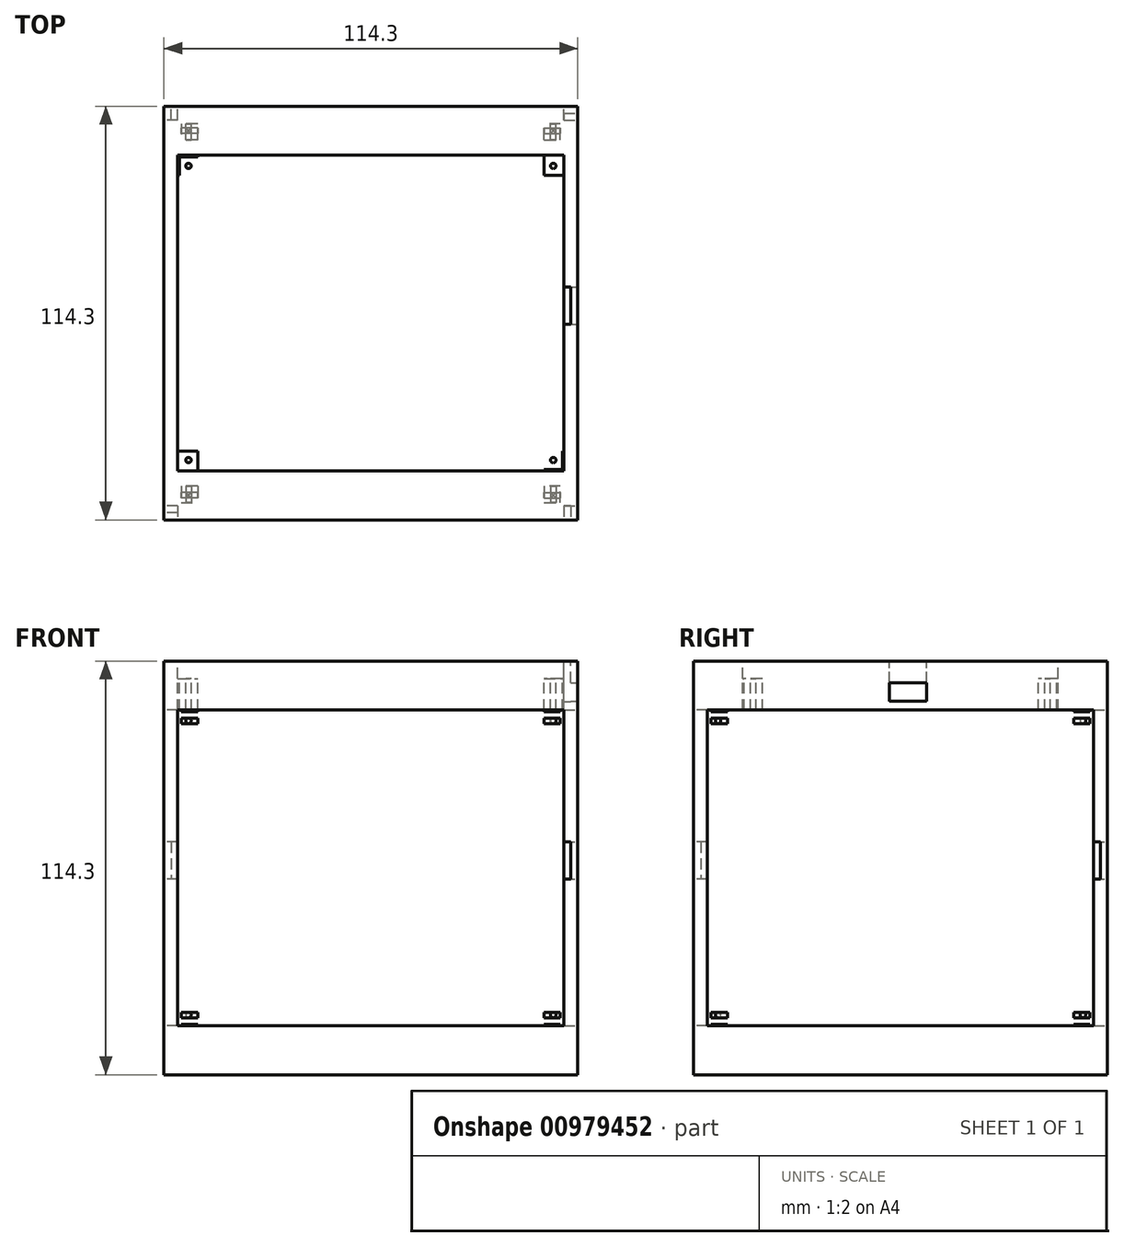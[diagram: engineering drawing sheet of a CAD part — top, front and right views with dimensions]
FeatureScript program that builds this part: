
annotation { "Feature Type Name" : "Feature", "Feature Type Description" : "" }
export const myFeature = defineFeature(function(context is Context, id is Id, definition is map)
    precondition{}
    {
        {
            var Q0;
            Q0=qCreatedBy(makeId("Top.planeOp"),FACE);
            var sketch = newSketch(context, id + "F0", { "sketchPlane" : qUnion([Q0])});
            skLineSegment(sketch, "E0.bottom", {"start": v(57.15, -57.15) * mm, "end": v(-57.15, -57.15) * mm});
            skLineSegment(sketch, "E0.top", {"start": v(57.15, 57.15) * mm, "end": v(-57.15, 57.15) * mm});
            skLineSegment(sketch, "E0.left", {"start": v(57.15, -57.15) * mm, "end": v(57.15, 57.15) * mm});
            skLineSegment(sketch, "E0.right", {"start": v(-57.15, -57.15) * mm, "end": v(-57.15, 57.15) * mm});
            skSolve(sketch);
        }
        {
            var Q0;
            Q0=makeQuery(id+"F0.imprint","IMPRINT",FACE,{"disambiguationData":[TD([[makeQuery(id+"F0.imprint","IMPRINT",EDGE,{"derivedFrom":sQuery(id+"F0.wireOp",EDGE,"E0.bottom")}),-1.0]])]});
            extrude(context, id + "F1", {"entities" : qUnion([Q0]), "depth" : 114.3 * mm, "offsetDistance" : 25.4 * mm});
        }
        {
            var Q0;
            Q0=makeQuery(id+"F1.opExtrude","CAP_FACE",FACE,{"disambiguationData":[OSD([sQuery(id+"F0.wireOp",EDGE,"E0.bottom"),sQuery(id+"F0.wireOp",EDGE,"E0.top"),sQuery(id+"F0.wireOp",EDGE,"E0.left"),sQuery(id+"F0.wireOp",EDGE,"E0.right")])],"isStart":false});
            var sketch = newSketch(context, id + "F2", { "sketchPlane" : qUnion([Q0])});
            skLineSegment(sketch, "E1.bottom", {"start": v(-52.92, 43.18) * mm, "end": v(52.92, 43.18) * mm});
            skLineSegment(sketch, "E1.top", {"start": v(-52.92, -43.18) * mm, "end": v(52.92, -43.18) * mm});
            skLineSegment(sketch, "E1.left", {"start": v(-52.92, 43.18) * mm, "end": v(-52.92, -43.18) * mm});
            skLineSegment(sketch, "E1.right", {"start": v(52.92, 43.18) * mm, "end": v(52.92, -43.18) * mm});
            skPoint(sketch, "E1.middle", {"position": v(0, 0) * mm});
            skCircle(sketch, "E2", {"center": v(-50.38, -40.64) * mm, "radius": 0.76 * mm});
            skCircle(sketch, "E3.MirrorC", {"center": v(50.38, -40.64) * mm, "radius": 0.76 * mm});
            skCircle(sketch, "E4.MirrorC", {"center": v(-50.38, 40.64) * mm, "radius": 0.76 * mm});
            skCircle(sketch, "E5.MirrorC", {"center": v(50.38, 40.64) * mm, "radius": 0.76 * mm});
            skLineSegment(sketch, "E6.0", {"start": v(-53.32, 43.58) * mm, "end": v(-53.32, -43.58) * mm});
            skLineSegment(sketch, "E6.1", {"start": v(-53.32, 43.58) * mm, "end": v(53.32, 43.58) * mm});
            skLineSegment(sketch, "E6.2", {"start": v(53.32, 43.58) * mm, "end": v(53.32, -43.58) * mm});
            skLineSegment(sketch, "E6.3", {"start": v(-53.32, -43.58) * mm, "end": v(53.32, -43.58) * mm});
            skLineSegment(sketch, "E7.top", {"start": v(53.32, -38.1) * mm, "end": v(47.84, -38.1) * mm});
            skLineSegment(sketch, "E7.right", {"start": v(47.84, -43.58) * mm, "end": v(47.84, -38.1) * mm});
            skLineSegment(sketch, "E8.MirrorCS", {"start": v(47.84, 43.58) * mm, "end": v(47.84, 38.1) * mm});
            skLineSegment(sketch, "E9.MirrorCS", {"start": v(53.32, 38.1) * mm, "end": v(47.84, 38.1) * mm});
            skLineSegment(sketch, "E10.MirrorCS", {"start": v(-53.32, -38.1) * mm, "end": v(-47.84, -38.1) * mm});
            skLineSegment(sketch, "E11.MirrorCS", {"start": v(-47.84, -43.58) * mm, "end": v(-47.84, -38.1) * mm});
            skLineSegment(sketch, "E12.MirrorCS", {"start": v(-53.32, 38.1) * mm, "end": v(-47.84, 38.1) * mm});
            skLineSegment(sketch, "E13.MirrorCS", {"start": v(-47.84, 43.58) * mm, "end": v(-47.84, 38.1) * mm});
            skLineSegment(sketch, "E14.MirrorCS", {"start": v(51.04, 6.8) * mm, "end": v(54.8, 6.8) * mm});
            skLineSegment(sketch, "E15.MirrorCS", {"start": v(51.04, -3.13) * mm, "end": v(55.2, -3.13) * mm});
            skLineSegment(sketch, "E16.MirrorCS", {"start": v(51.04, -2.73) * mm, "end": v(54.8, -2.73) * mm});
            skLineSegment(sketch, "E17.MirrorCS", {"start": v(55.2, 7.2) * mm, "end": v(55.2, -3.13) * mm});
            skLineSegment(sketch, "E18.MirrorCS", {"start": v(51.04, 7.2) * mm, "end": v(55.2, 7.2) * mm});
            skLineSegment(sketch, "E19.MirrorCS", {"start": v(54.8, 6.8) * mm, "end": v(54.8, -2.73) * mm});
            skPoint(sketch, "E20.MirrorP", {"position": v(52.92, 2.03) * mm});
            skLineSegment(sketch, "E21.bottom", {"start": v(-57.15, -57.15) * mm, "end": v(57.15, -57.15) * mm});
            skLineSegment(sketch, "E21.top", {"start": v(-57.15, 57.15) * mm, "end": v(57.15, 57.15) * mm});
            skLineSegment(sketch, "E21.left", {"start": v(-57.15, -57.15) * mm, "end": v(-57.15, 57.15) * mm});
            skLineSegment(sketch, "E21.right", {"start": v(57.15, -57.15) * mm, "end": v(57.15, 57.15) * mm});
            skSolve(sketch);
        }
        {
            var Q0;
            Q0=makeQuery(id+"F2.imprint","IMPRINT",FACE,{"disambiguationData":[TD([[makeQuery(id+"F2.imprint","IMPRINT",EDGE,{"derivedFrom":sQuery(id+"F2.wireOp",EDGE,"E2")}),-1.0]])]});
            var Q1;
            {var subQ5=sQuery(id+"F2.wireOp",EDGE,"E1.left");var subQ6=sQuery(id+"F2.wireOp",EDGE,"E1.top");var subQ7=makeQuery(id+"F2.imprint","INTERSECT",VERTEX,{"derivedFrom":[subQ6,subQ5]});Q1=makeQuery(id+"F2.imprint","IMPRINT",FACE,{"disambiguationData":[TD([[makeQuery(id+"F2.imprint","IMPRINT",EDGE,{"disambiguationData":[TD([[subQ7,-1.0]])],"derivedFrom":subQ6}),-1.0]])]});}
            var Q2;
            {var subQ7=sQuery(id+"F2.wireOp",EDGE,"E1.right");var subQ8=sQuery(id+"F2.wireOp",EDGE,"E1.top");var subQ9=makeQuery(id+"F2.imprint","INTERSECT",VERTEX,{"derivedFrom":[subQ8,subQ7]});Q2=makeQuery(id+"F2.imprint","IMPRINT",FACE,{"disambiguationData":[TD([[makeQuery(id+"F2.imprint","IMPRINT",EDGE,{"disambiguationData":[TD([[subQ9,1.0]])],"derivedFrom":subQ8}),-1.0]])]});}
            var Q3;
            Q3=makeQuery(id+"F2.imprint","IMPRINT",FACE,{"disambiguationData":[TD([[makeQuery(id+"F2.imprint","IMPRINT",EDGE,{"derivedFrom":sQuery(id+"F2.wireOp",EDGE,"E3.MirrorC")}),1.0]])]});
            var Q4;
            {var subQ7=sQuery(id+"F2.wireOp",EDGE,"E1.right");var subQ8=sQuery(id+"F2.wireOp",EDGE,"E1.bottom");var subQ9=makeQuery(id+"F2.imprint","INTERSECT",VERTEX,{"derivedFrom":[subQ8,subQ7]});Q4=makeQuery(id+"F2.imprint","IMPRINT",FACE,{"disambiguationData":[TD([[makeQuery(id+"F2.imprint","IMPRINT",EDGE,{"disambiguationData":[TD([[subQ9,1.0]])],"derivedFrom":subQ8}),1.0]])]});}
            var Q5;
            Q5=makeQuery(id+"F2.imprint","IMPRINT",FACE,{"disambiguationData":[TD([[makeQuery(id+"F2.imprint","IMPRINT",EDGE,{"derivedFrom":sQuery(id+"F2.wireOp",EDGE,"E5.MirrorC")}),-1.0]])]});
            var Q6;
            {var subQ5=sQuery(id+"F2.wireOp",EDGE,"E1.left");var subQ6=sQuery(id+"F2.wireOp",EDGE,"E1.bottom");var subQ7=makeQuery(id+"F2.imprint","INTERSECT",VERTEX,{"derivedFrom":[subQ6,subQ5]});Q6=makeQuery(id+"F2.imprint","IMPRINT",FACE,{"disambiguationData":[TD([[makeQuery(id+"F2.imprint","IMPRINT",EDGE,{"disambiguationData":[TD([[subQ7,-1.0]])],"derivedFrom":subQ6}),1.0]])]});}
            var Q7;
            Q7=makeQuery(id+"F2.imprint","IMPRINT",FACE,{"disambiguationData":[TD([[makeQuery(id+"F2.imprint","IMPRINT",EDGE,{"derivedFrom":sQuery(id+"F2.wireOp",EDGE,"E4.MirrorC")}),1.0]])]});
            extrude(context, id + "F3", {"entities" : qUnion([Q0, Q1, Q2, Q3, Q4, Q5, Q6, Q7]), "operationType" : NewBodyOperationType.REMOVE, "oppositeDirection" : true, "depth" : 4.83 * mm, "offsetDistance" : 25.4 * mm});
        }
        {
            var Q0;
            Q0=makeQuery(id+"F2.imprint","IMPRINT",FACE,{"disambiguationData":[TD([[makeQuery(id+"F2.imprint","IMPRINT",EDGE,{"derivedFrom":sQuery(id+"F2.wireOp",EDGE,"E4.MirrorC")}),-1.0]])]});
            var Q1;
            {var subQ20=sQuery(id+"F2.wireOp",EDGE,"E1.bottom");var subQ22=sQuery(id+"F2.wireOp",EDGE,"E13.MirrorCS");var subQ23=makeQuery(id+"F2.imprint","INTERSECT",VERTEX,{"derivedFrom":[subQ20,subQ22]});Q1=makeQuery(id+"F2.imprint","IMPRINT",FACE,{"disambiguationData":[TD([[makeQuery(id+"F2.imprint","IMPRINT",EDGE,{"disambiguationData":[TD([[subQ23,-1.0]])],"derivedFrom":subQ20}),-1.0]])]});}
            var Q2;
            {var subQ0=sQuery(id+"F2.wireOp",EDGE,"E13.MirrorCS");var subQ1=sQuery(id+"F2.wireOp",EDGE,"E1.bottom");var subQ2=makeQuery(id+"F2.imprint","INTERSECT",VERTEX,{"derivedFrom":[subQ1,subQ0]});Q2=makeQuery(id+"F2.imprint","IMPRINT",FACE,{"disambiguationData":[TD([[makeQuery(id+"F2.imprint","IMPRINT",EDGE,{"disambiguationData":[TD([[subQ2,-1.0]])],"derivedFrom":subQ1}),1.0]])]});}
            var Q3;
            {var subQ0=sQuery(id+"F2.wireOp",EDGE,"59694670-6818-448a-b48b-58002c6f26f5.2");var subQ1=sQuery(id+"F2.wireOp",EDGE,"E1.left");var subQ2=makeQuery(id+"F2.imprint","INTERSECT",VERTEX,{"derivedFrom":[subQ1,subQ0]});Q3=makeQuery(id+"F2.imprint","IMPRINT",FACE,{"disambiguationData":[TD([[makeQuery(id+"F2.imprint","IMPRINT",EDGE,{"disambiguationData":[TD([[subQ2,1.0]])],"derivedFrom":subQ1}),-1.0]])]});}
            var Q4;
            Q4=makeQuery(id+"F2.imprint","IMPRINT",FACE,{"disambiguationData":[TD([[makeQuery(id+"F2.imprint","IMPRINT",EDGE,{"derivedFrom":sQuery(id+"F2.wireOp",EDGE,"E5.MirrorC")}),1.0]])]});
            var Q5;
            {var subQ0=sQuery(id+"F2.wireOp",EDGE,"E9.MirrorCS");var subQ1=sQuery(id+"F2.wireOp",EDGE,"E1.right");var subQ2=makeQuery(id+"F2.imprint","INTERSECT",VERTEX,{"derivedFrom":[subQ1,subQ0]});Q5=makeQuery(id+"F2.imprint","IMPRINT",FACE,{"disambiguationData":[TD([[makeQuery(id+"F2.imprint","IMPRINT",EDGE,{"disambiguationData":[TD([[subQ2,-1.0]])],"derivedFrom":subQ1}),1.0]])]});}
            var Q6;
            Q6=makeQuery(id+"F2.imprint","IMPRINT",FACE,{"disambiguationData":[TD([[makeQuery(id+"F2.imprint","IMPRINT",EDGE,{"derivedFrom":sQuery(id+"F2.wireOp",EDGE,"E3.MirrorC")}),-1.0]])]});
            var Q7;
            {var subQ0=sQuery(id+"F2.wireOp",EDGE,"E11.MirrorCS");var subQ1=sQuery(id+"F2.wireOp",EDGE,"E1.top");var subQ2=makeQuery(id+"F2.imprint","INTERSECT",VERTEX,{"derivedFrom":[subQ1,subQ0]});Q7=makeQuery(id+"F2.imprint","IMPRINT",FACE,{"disambiguationData":[TD([[makeQuery(id+"F2.imprint","IMPRINT",EDGE,{"disambiguationData":[TD([[subQ2,-1.0]])],"derivedFrom":subQ1}),-1.0]])]});}
            var Q8;
            Q8=makeQuery(id+"F2.imprint","IMPRINT",FACE,{"disambiguationData":[TD([[makeQuery(id+"F2.imprint","IMPRINT",EDGE,{"derivedFrom":sQuery(id+"F2.wireOp",EDGE,"E2")}),1.0]])]});
            var Q9;
            {var subQ0=sQuery(id+"F2.wireOp",EDGE,"01Z94Qzt-EJPi-t4h5-vXe4-wsMJar4ZymQo.bottom");var subQ1=sQuery(id+"F2.wireOp",EDGE,"E1.left");var subQ2=makeQuery(id+"F2.imprint","INTERSECT",VERTEX,{"derivedFrom":[subQ1,subQ0]});Q9=makeQuery(id+"F2.imprint","IMPRINT",FACE,{"disambiguationData":[TD([[makeQuery(id+"F2.imprint","IMPRINT",EDGE,{"disambiguationData":[TD([[subQ2,-1.0]])],"derivedFrom":subQ1}),-1.0]])]});}
            var Q10;
            {var subQ0=sQuery(id+"F2.wireOp",EDGE,"59694670-6818-448a-b48b-58002c6f26f5.2");var subQ1=sQuery(id+"F2.wireOp",EDGE,"E1.left");var subQ2=makeQuery(id+"F2.imprint","INTERSECT",VERTEX,{"derivedFrom":[subQ1,subQ0]});Q10=makeQuery(id+"F2.imprint","IMPRINT",FACE,{"disambiguationData":[TD([[makeQuery(id+"F2.imprint","IMPRINT",EDGE,{"disambiguationData":[TD([[subQ2,-1.0]])],"derivedFrom":subQ1}),-1.0]])]});}
            var Q11;
            {var subQ0=sQuery(id+"F2.wireOp",EDGE,"01Z94Qzt-EJPi-t4h5-vXe4-wsMJar4ZymQo.top");var subQ1=sQuery(id+"F2.wireOp",EDGE,"E1.left");var subQ2=makeQuery(id+"F2.imprint","INTERSECT",VERTEX,{"derivedFrom":[subQ1,subQ0]});Q11=makeQuery(id+"F2.imprint","IMPRINT",FACE,{"disambiguationData":[TD([[makeQuery(id+"F2.imprint","IMPRINT",EDGE,{"disambiguationData":[TD([[subQ2,-1.0]])],"derivedFrom":subQ1}),-1.0]])]});}
            var Q12;
            {var subQ0=sQuery(id+"F2.wireOp",EDGE,"59694670-6818-448a-b48b-58002c6f26f5.0");var subQ1=sQuery(id+"F2.wireOp",EDGE,"E1.left");var subQ2=makeQuery(id+"F2.imprint","INTERSECT",VERTEX,{"derivedFrom":[subQ1,subQ0]});Q12=makeQuery(id+"F2.imprint","IMPRINT",FACE,{"disambiguationData":[TD([[makeQuery(id+"F2.imprint","IMPRINT",EDGE,{"disambiguationData":[TD([[subQ2,-1.0]])],"derivedFrom":subQ1}),-1.0]])]});}
            var Q13;
            {var subQ0=sQuery(id+"F2.wireOp",EDGE,"E18.MirrorCS");var subQ1=sQuery(id+"F2.wireOp",EDGE,"E1.right");var subQ2=makeQuery(id+"F2.imprint","INTERSECT",VERTEX,{"derivedFrom":[subQ1,subQ0]});Q13=makeQuery(id+"F2.imprint","IMPRINT",FACE,{"disambiguationData":[TD([[makeQuery(id+"F2.imprint","IMPRINT",EDGE,{"disambiguationData":[TD([[subQ2,-1.0]])],"derivedFrom":subQ1}),1.0]])]});}
            var Q14;
            {var subQ0=sQuery(id+"F2.wireOp",EDGE,"E14.MirrorCS");var subQ1=sQuery(id+"F2.wireOp",EDGE,"E1.right");var subQ2=makeQuery(id+"F2.imprint","INTERSECT",VERTEX,{"derivedFrom":[subQ1,subQ0]});Q14=makeQuery(id+"F2.imprint","IMPRINT",FACE,{"disambiguationData":[TD([[makeQuery(id+"F2.imprint","IMPRINT",EDGE,{"disambiguationData":[TD([[subQ2,-1.0]])],"derivedFrom":subQ1}),1.0]])]});}
            var Q15;
            {var subQ0=sQuery(id+"F2.wireOp",EDGE,"E16.MirrorCS");var subQ1=sQuery(id+"F2.wireOp",EDGE,"E1.right");var subQ2=makeQuery(id+"F2.imprint","INTERSECT",VERTEX,{"derivedFrom":[subQ1,subQ0]});Q15=makeQuery(id+"F2.imprint","IMPRINT",FACE,{"disambiguationData":[TD([[makeQuery(id+"F2.imprint","IMPRINT",EDGE,{"disambiguationData":[TD([[subQ2,-1.0]])],"derivedFrom":subQ1}),1.0]])]});}
            var Q16;
            {var subQ0=sQuery(id+"F2.wireOp",EDGE,"E15.MirrorCS");var subQ1=sQuery(id+"F2.wireOp",EDGE,"E1.right");var subQ2=makeQuery(id+"F2.imprint","INTERSECT",VERTEX,{"derivedFrom":[subQ1,subQ0]});Q16=makeQuery(id+"F2.imprint","IMPRINT",FACE,{"disambiguationData":[TD([[makeQuery(id+"F2.imprint","IMPRINT",EDGE,{"disambiguationData":[TD([[subQ2,-1.0]])],"derivedFrom":subQ1}),1.0]])]});}
            extrude(context, id + "F4", {"entities" : qUnion([Q0, Q1, Q2, Q3, Q4, Q5, Q6, Q7, Q8, Q9, Q10, Q11, Q12, Q13, Q14, Q15, Q16]), "operationType" : NewBodyOperationType.REMOVE, "oppositeDirection" : true, "depth" : 25.4 * mm, "offsetDistance" : 25.4 * mm});
        }
        {
            var Q0;
            Q0=makeQuery(id+"F1.opExtrude","SWEPT_FACE",FACE,{"disambiguationData":[OSD([sQuery(id+"F0.wireOp",EDGE,"E0.left")])]});
            var sketch = newSketch(context, id + "F5", { "sketchPlane" : qUnion([Q0])});
            skLineSegment(sketch, "E22.bottom", {"start": v(-3.13, 114.3) * mm, "end": v(7.2, 114.3) * mm});
            skLineSegment(sketch, "E22.top", {"start": v(-3.13, 108.32) * mm, "end": v(7.2, 108.32) * mm});
            skLineSegment(sketch, "E22.left", {"start": v(-3.13, 114.3) * mm, "end": v(-3.13, 108.32) * mm});
            skLineSegment(sketch, "E22.right", {"start": v(7.2, 114.3) * mm, "end": v(7.2, 108.32) * mm});
            skLineSegment(sketch, "E23.top", {"start": v(-3.13, 103.16) * mm, "end": v(7.2, 103.16) * mm});
            skLineSegment(sketch, "E23.left", {"start": v(-3.13, 114.3) * mm, "end": v(-3.13, 103.16) * mm});
            skLineSegment(sketch, "E23.right", {"start": v(7.2, 114.3) * mm, "end": v(7.2, 103.16) * mm});
            skSolve(sketch);
        }
        {
            var Q0;
            {var subQ5=sQuery(id+"F2.wireOp",EDGE,"E19.MirrorCS");Q0=makeQuery(id+"F2.imprint","IMPRINT",FACE,{"disambiguationData":[TD([[makeQuery(id+"F2.imprint","IMPRINT",EDGE,{"derivedFrom":subQ5}),-1.0]])]});}
            var Q1;
            {var subQ0=sQuery(id+"F2.wireOp",EDGE,"E17.MirrorCS");Q1=makeQuery(id+"F2.imprint","IMPRINT",FACE,{"disambiguationData":[TD([[makeQuery(id+"F2.imprint","IMPRINT",EDGE,{"derivedFrom":subQ0}),-1.0]])]});}
            extrude(context, id + "F6", {"entities" : qUnion([Q0, Q1]), "operationType" : NewBodyOperationType.REMOVE, "oppositeDirection" : true, "depth" : 11.17 * mm, "offsetDistance" : 25.4 * mm});
        }
        {
            var Q0;
            Q0=makeQuery(id+"F5.imprint","IMPRINT",FACE,{"disambiguationData":[TD([[makeQuery(id+"F5.imprint","IMPRINT",EDGE,{"derivedFrom":sQuery(id+"F5.wireOp",EDGE,"E22.top")}),-1.0]])]});
            extrude(context, id + "F7", {"entities" : qUnion([Q0]), "operationType" : NewBodyOperationType.REMOVE, "oppositeDirection" : true, "depth" : 25.4 * mm, "offsetDistance" : 25.4 * mm});
        }
        {
            var Q0;
            Q0=makeQuery(id+"F1.opExtrude","SWEPT_FACE",FACE,{"disambiguationData":[OSD([sQuery(id+"F0.wireOp",EDGE,"E0.bottom")])]});
            var sketch = newSketch(context, id + "F8", { "sketchPlane" : qUnion([Q0])});
            skLineSegment(sketch, "E24.bottom", {"start": v(-52.92, 100.33) * mm, "end": v(52.92, 100.33) * mm});
            skLineSegment(sketch, "E24.top", {"start": v(-52.92, 13.97) * mm, "end": v(52.92, 13.97) * mm});
            skLineSegment(sketch, "E24.left", {"start": v(-52.92, 100.33) * mm, "end": v(-52.92, 13.97) * mm});
            skLineSegment(sketch, "E24.right", {"start": v(52.92, 100.33) * mm, "end": v(52.92, 13.97) * mm});
            skPoint(sketch, "E24.middle", {"position": v(0, 57.15) * mm});
            skCircle(sketch, "E25", {"center": v(-50.38, 16.51) * mm, "radius": 0.76 * mm});
            skCircle(sketch, "E26.MirrorC", {"center": v(50.38, 16.51) * mm, "radius": 0.76 * mm});
            skCircle(sketch, "E27.MirrorC", {"center": v(-50.38, 97.8) * mm, "radius": 0.76 * mm});
            skCircle(sketch, "E28.MirrorC", {"center": v(50.38, 97.8) * mm, "radius": 0.76 * mm});
            skLineSegment(sketch, "E29.0", {"start": v(-53.32, 100.73) * mm, "end": v(-53.32, 13.57) * mm});
            skLineSegment(sketch, "E29.1", {"start": v(-53.32, 100.73) * mm, "end": v(53.32, 100.73) * mm});
            skLineSegment(sketch, "E29.2", {"start": v(53.32, 100.73) * mm, "end": v(53.32, 13.57) * mm});
            skLineSegment(sketch, "E29.3", {"start": v(-53.32, 13.57) * mm, "end": v(53.32, 13.57) * mm});
            skLineSegment(sketch, "E30.top", {"start": v(53.32, 19.05) * mm, "end": v(47.84, 19.05) * mm});
            skLineSegment(sketch, "E30.right", {"start": v(47.84, 13.57) * mm, "end": v(47.84, 19.05) * mm});
            skLineSegment(sketch, "E31.MirrorCS", {"start": v(47.84, 100.73) * mm, "end": v(47.84, 95.25) * mm});
            skLineSegment(sketch, "E32.MirrorCS", {"start": v(53.32, 95.25) * mm, "end": v(47.84, 95.25) * mm});
            skLineSegment(sketch, "E33.MirrorCS", {"start": v(-53.32, 19.05) * mm, "end": v(-47.84, 19.05) * mm});
            skLineSegment(sketch, "E34.MirrorCS", {"start": v(-47.84, 13.57) * mm, "end": v(-47.84, 19.05) * mm});
            skLineSegment(sketch, "E35.MirrorCS", {"start": v(-53.32, 95.25) * mm, "end": v(-47.84, 95.25) * mm});
            skLineSegment(sketch, "E36.MirrorCS", {"start": v(-47.84, 100.73) * mm, "end": v(-47.84, 95.25) * mm});
            skLineSegment(sketch, "E37.MirrorCS", {"start": v(51.04, 63.94) * mm, "end": v(54.8, 63.94) * mm});
            skLineSegment(sketch, "E38.MirrorCS", {"start": v(51.04, 54.02) * mm, "end": v(55.2, 54.02) * mm});
            skLineSegment(sketch, "E39.MirrorCS", {"start": v(51.04, 54.42) * mm, "end": v(54.8, 54.42) * mm});
            skLineSegment(sketch, "E40.MirrorCS", {"start": v(55.2, 64.34) * mm, "end": v(55.2, 54.02) * mm});
            skLineSegment(sketch, "E41.MirrorCS", {"start": v(51.04, 64.34) * mm, "end": v(55.2, 64.34) * mm});
            skLineSegment(sketch, "E42.MirrorCS", {"start": v(54.8, 63.94) * mm, "end": v(54.8, 54.42) * mm});
            skPoint(sketch, "E43.MirrorP", {"position": v(52.92, 59.18) * mm});
            skLineSegment(sketch, "E44.bottom", {"start": v(-57.15, 0) * mm, "end": v(57.15, 0) * mm});
            skLineSegment(sketch, "E44.top", {"start": v(-57.15, 114.3) * mm, "end": v(57.15, 114.3) * mm});
            skLineSegment(sketch, "E44.left", {"start": v(-57.15, 0) * mm, "end": v(-57.15, 114.3) * mm});
            skLineSegment(sketch, "E44.right", {"start": v(57.15, 0) * mm, "end": v(57.15, 114.3) * mm});
            skSolve(sketch);
        }
        {
            var Q0;
            Q0=makeQuery(id+"F1.opExtrude","SWEPT_FACE",FACE,{"disambiguationData":[OSD([sQuery(id+"F0.wireOp",EDGE,"E0.left")])]});
            var sketch = newSketch(context, id + "F9", { "sketchPlane" : qUnion([Q0])});
            skLineSegment(sketch, "E45.bottom", {"start": v(-52.92, 100.33) * mm, "end": v(52.92, 100.33) * mm});
            skLineSegment(sketch, "E45.top", {"start": v(-52.92, 13.97) * mm, "end": v(52.92, 13.97) * mm});
            skLineSegment(sketch, "E45.left", {"start": v(-52.92, 100.33) * mm, "end": v(-52.92, 13.97) * mm});
            skLineSegment(sketch, "E45.right", {"start": v(52.92, 100.33) * mm, "end": v(52.92, 13.97) * mm});
            skPoint(sketch, "E45.middle", {"position": v(0, 57.15) * mm});
            skCircle(sketch, "E46", {"center": v(-50.38, 16.51) * mm, "radius": 0.76 * mm});
            skCircle(sketch, "E47.MirrorC", {"center": v(50.38, 16.51) * mm, "radius": 0.76 * mm});
            skCircle(sketch, "E48.MirrorC", {"center": v(-50.38, 97.8) * mm, "radius": 0.76 * mm});
            skCircle(sketch, "E49.MirrorC", {"center": v(50.38, 97.8) * mm, "radius": 0.76 * mm});
            skLineSegment(sketch, "E50.0", {"start": v(-53.32, 100.73) * mm, "end": v(-53.32, 13.57) * mm});
            skLineSegment(sketch, "E50.1", {"start": v(-53.32, 100.73) * mm, "end": v(53.32, 100.73) * mm});
            skLineSegment(sketch, "E50.2", {"start": v(53.32, 100.73) * mm, "end": v(53.32, 13.57) * mm});
            skLineSegment(sketch, "E50.3", {"start": v(-53.32, 13.57) * mm, "end": v(53.32, 13.57) * mm});
            skLineSegment(sketch, "E51.top", {"start": v(53.32, 19.05) * mm, "end": v(47.84, 19.05) * mm});
            skLineSegment(sketch, "E51.right", {"start": v(47.84, 13.57) * mm, "end": v(47.84, 19.05) * mm});
            skLineSegment(sketch, "E52.MirrorCS", {"start": v(47.84, 100.73) * mm, "end": v(47.84, 95.25) * mm});
            skLineSegment(sketch, "E53.MirrorCS", {"start": v(53.32, 95.25) * mm, "end": v(47.84, 95.25) * mm});
            skLineSegment(sketch, "E54.MirrorCS", {"start": v(-53.32, 19.05) * mm, "end": v(-47.84, 19.05) * mm});
            skLineSegment(sketch, "E55.MirrorCS", {"start": v(-47.84, 13.57) * mm, "end": v(-47.84, 19.05) * mm});
            skLineSegment(sketch, "E56.MirrorCS", {"start": v(-53.32, 95.25) * mm, "end": v(-47.84, 95.25) * mm});
            skLineSegment(sketch, "E57.MirrorCS", {"start": v(-47.84, 100.73) * mm, "end": v(-47.84, 95.25) * mm});
            skLineSegment(sketch, "E58.MirrorCS", {"start": v(51.04, 63.94) * mm, "end": v(54.8, 63.94) * mm});
            skLineSegment(sketch, "E59.MirrorCS", {"start": v(51.04, 54.02) * mm, "end": v(55.2, 54.02) * mm});
            skLineSegment(sketch, "E60.MirrorCS", {"start": v(51.04, 54.42) * mm, "end": v(54.8, 54.42) * mm});
            skLineSegment(sketch, "E61.MirrorCS", {"start": v(55.2, 64.34) * mm, "end": v(55.2, 54.02) * mm});
            skLineSegment(sketch, "E62.MirrorCS", {"start": v(51.04, 64.34) * mm, "end": v(55.2, 64.34) * mm});
            skLineSegment(sketch, "E63.MirrorCS", {"start": v(54.8, 63.94) * mm, "end": v(54.8, 54.42) * mm});
            skPoint(sketch, "E64.MirrorP", {"position": v(52.92, 59.18) * mm});
            skLineSegment(sketch, "E65.bottom", {"start": v(-57.15, 0) * mm, "end": v(57.15, 0) * mm});
            skLineSegment(sketch, "E65.top", {"start": v(-57.15, 114.3) * mm, "end": v(57.15, 114.3) * mm});
            skLineSegment(sketch, "E65.left", {"start": v(-57.15, 0) * mm, "end": v(-57.15, 114.3) * mm});
            skLineSegment(sketch, "E65.right", {"start": v(57.15, 0) * mm, "end": v(57.15, 114.3) * mm});
            skSolve(sketch);
        }
        {
            var Q0;
            Q0=makeQuery(id+"F1.opExtrude","SWEPT_FACE",FACE,{"disambiguationData":[OSD([sQuery(id+"F0.wireOp",EDGE,"E0.top")])]});
            var sketch = newSketch(context, id + "F10", { "sketchPlane" : qUnion([Q0])});
            skLineSegment(sketch, "E66.bottom", {"start": v(-52.92, 100.33) * mm, "end": v(52.92, 100.33) * mm});
            skLineSegment(sketch, "E66.top", {"start": v(-52.92, 13.97) * mm, "end": v(52.92, 13.97) * mm});
            skLineSegment(sketch, "E66.left", {"start": v(-52.92, 100.33) * mm, "end": v(-52.92, 13.97) * mm});
            skLineSegment(sketch, "E66.right", {"start": v(52.92, 100.33) * mm, "end": v(52.92, 13.97) * mm});
            skPoint(sketch, "E66.middle", {"position": v(0, 57.15) * mm});
            skCircle(sketch, "E67", {"center": v(-50.38, 16.51) * mm, "radius": 0.76 * mm});
            skCircle(sketch, "E68.MirrorC", {"center": v(50.38, 16.51) * mm, "radius": 0.76 * mm});
            skCircle(sketch, "E69.MirrorC", {"center": v(-50.38, 97.8) * mm, "radius": 0.76 * mm});
            skCircle(sketch, "E70.MirrorC", {"center": v(50.38, 97.8) * mm, "radius": 0.76 * mm});
            skLineSegment(sketch, "E71.0", {"start": v(-53.32, 100.73) * mm, "end": v(-53.32, 13.57) * mm});
            skLineSegment(sketch, "E71.1", {"start": v(-53.32, 100.73) * mm, "end": v(53.32, 100.73) * mm});
            skLineSegment(sketch, "E71.2", {"start": v(53.32, 100.73) * mm, "end": v(53.32, 13.57) * mm});
            skLineSegment(sketch, "E71.3", {"start": v(-53.32, 13.57) * mm, "end": v(53.32, 13.57) * mm});
            skLineSegment(sketch, "E72.top", {"start": v(53.32, 19.05) * mm, "end": v(47.84, 19.05) * mm});
            skLineSegment(sketch, "E72.right", {"start": v(47.84, 13.57) * mm, "end": v(47.84, 19.05) * mm});
            skLineSegment(sketch, "E73.MirrorCS", {"start": v(47.84, 100.73) * mm, "end": v(47.84, 95.25) * mm});
            skLineSegment(sketch, "E74.MirrorCS", {"start": v(53.32, 95.25) * mm, "end": v(47.84, 95.25) * mm});
            skLineSegment(sketch, "E75.MirrorCS", {"start": v(-53.32, 19.05) * mm, "end": v(-47.84, 19.05) * mm});
            skLineSegment(sketch, "E76.MirrorCS", {"start": v(-47.84, 13.57) * mm, "end": v(-47.84, 19.05) * mm});
            skLineSegment(sketch, "E77.MirrorCS", {"start": v(-53.32, 95.25) * mm, "end": v(-47.84, 95.25) * mm});
            skLineSegment(sketch, "E78.MirrorCS", {"start": v(-47.84, 100.73) * mm, "end": v(-47.84, 95.25) * mm});
            skLineSegment(sketch, "E79.MirrorCS", {"start": v(51.04, 63.94) * mm, "end": v(54.8, 63.94) * mm});
            skLineSegment(sketch, "E80.MirrorCS", {"start": v(51.04, 54.02) * mm, "end": v(55.2, 54.02) * mm});
            skLineSegment(sketch, "E81.MirrorCS", {"start": v(51.04, 54.42) * mm, "end": v(54.8, 54.42) * mm});
            skLineSegment(sketch, "E82.MirrorCS", {"start": v(55.2, 64.34) * mm, "end": v(55.2, 54.02) * mm});
            skLineSegment(sketch, "E83.MirrorCS", {"start": v(51.04, 64.34) * mm, "end": v(55.2, 64.34) * mm});
            skLineSegment(sketch, "E84.MirrorCS", {"start": v(54.8, 63.94) * mm, "end": v(54.8, 54.42) * mm});
            skPoint(sketch, "E85.MirrorP", {"position": v(52.92, 59.18) * mm});
            skLineSegment(sketch, "E86.bottom", {"start": v(-57.15, 0) * mm, "end": v(57.15, 0) * mm});
            skLineSegment(sketch, "E86.top", {"start": v(-57.15, 114.3) * mm, "end": v(57.15, 114.3) * mm});
            skLineSegment(sketch, "E86.left", {"start": v(-57.15, 0) * mm, "end": v(-57.15, 114.3) * mm});
            skLineSegment(sketch, "E86.right", {"start": v(57.15, 0) * mm, "end": v(57.15, 114.3) * mm});
            skSolve(sketch);
        }
        {
            var Q0;
            Q0=makeQuery(id+"F1.opExtrude","SWEPT_FACE",FACE,{"disambiguationData":[OSD([sQuery(id+"F0.wireOp",EDGE,"E0.right")])]});
            var sketch = newSketch(context, id + "F11", { "sketchPlane" : qUnion([Q0])});
            skLineSegment(sketch, "E87.bottom", {"start": v(-52.92, 100.33) * mm, "end": v(52.92, 100.33) * mm});
            skLineSegment(sketch, "E87.top", {"start": v(-52.92, 13.97) * mm, "end": v(52.92, 13.97) * mm});
            skLineSegment(sketch, "E87.left", {"start": v(-52.92, 100.33) * mm, "end": v(-52.92, 13.97) * mm});
            skLineSegment(sketch, "E87.right", {"start": v(52.92, 100.33) * mm, "end": v(52.92, 13.97) * mm});
            skPoint(sketch, "E87.middle", {"position": v(0, 57.15) * mm});
            skCircle(sketch, "E88", {"center": v(-50.38, 16.51) * mm, "radius": 0.76 * mm});
            skCircle(sketch, "E89.MirrorC", {"center": v(50.38, 16.51) * mm, "radius": 0.76 * mm});
            skCircle(sketch, "E90.MirrorC", {"center": v(-50.38, 97.8) * mm, "radius": 0.76 * mm});
            skCircle(sketch, "E91.MirrorC", {"center": v(50.38, 97.8) * mm, "radius": 0.76 * mm});
            skLineSegment(sketch, "E92.0", {"start": v(-53.32, 100.73) * mm, "end": v(-53.32, 13.57) * mm});
            skLineSegment(sketch, "E92.1", {"start": v(-53.32, 100.73) * mm, "end": v(53.32, 100.73) * mm});
            skLineSegment(sketch, "E92.2", {"start": v(53.32, 100.73) * mm, "end": v(53.32, 13.57) * mm});
            skLineSegment(sketch, "E92.3", {"start": v(-53.32, 13.57) * mm, "end": v(53.32, 13.57) * mm});
            skLineSegment(sketch, "E93.top", {"start": v(53.32, 19.05) * mm, "end": v(47.84, 19.05) * mm});
            skLineSegment(sketch, "E93.right", {"start": v(47.84, 13.57) * mm, "end": v(47.84, 19.05) * mm});
            skLineSegment(sketch, "E94.MirrorCS", {"start": v(47.84, 100.73) * mm, "end": v(47.84, 95.25) * mm});
            skLineSegment(sketch, "E95.MirrorCS", {"start": v(53.32, 95.25) * mm, "end": v(47.84, 95.25) * mm});
            skLineSegment(sketch, "E96.MirrorCS", {"start": v(-53.32, 19.05) * mm, "end": v(-47.84, 19.05) * mm});
            skLineSegment(sketch, "E97.MirrorCS", {"start": v(-47.84, 13.57) * mm, "end": v(-47.84, 19.05) * mm});
            skLineSegment(sketch, "E98.MirrorCS", {"start": v(-53.32, 95.25) * mm, "end": v(-47.84, 95.25) * mm});
            skLineSegment(sketch, "E99.MirrorCS", {"start": v(-47.84, 100.73) * mm, "end": v(-47.84, 95.25) * mm});
            skLineSegment(sketch, "E100.MirrorCS", {"start": v(51.04, 63.94) * mm, "end": v(54.8, 63.94) * mm});
            skLineSegment(sketch, "E101.MirrorCS", {"start": v(51.04, 54.02) * mm, "end": v(55.2, 54.02) * mm});
            skLineSegment(sketch, "E102.MirrorCS", {"start": v(51.04, 54.42) * mm, "end": v(54.8, 54.42) * mm});
            skLineSegment(sketch, "E103.MirrorCS", {"start": v(55.2, 64.34) * mm, "end": v(55.2, 54.02) * mm});
            skLineSegment(sketch, "E104.MirrorCS", {"start": v(51.04, 64.34) * mm, "end": v(55.2, 64.34) * mm});
            skLineSegment(sketch, "E105.MirrorCS", {"start": v(54.8, 63.94) * mm, "end": v(54.8, 54.42) * mm});
            skPoint(sketch, "E106.MirrorP", {"position": v(52.92, 59.18) * mm});
            skLineSegment(sketch, "E107.bottom", {"start": v(-57.15, 0) * mm, "end": v(57.15, 0) * mm});
            skLineSegment(sketch, "E107.top", {"start": v(-57.15, 114.3) * mm, "end": v(57.15, 114.3) * mm});
            skLineSegment(sketch, "E107.left", {"start": v(-57.15, 0) * mm, "end": v(-57.15, 114.3) * mm});
            skLineSegment(sketch, "E107.right", {"start": v(57.15, 0) * mm, "end": v(57.15, 114.3) * mm});
            skSolve(sketch);
        }
        {
            var Q0;
            Q0=makeQuery(id+"F11.imprint","IMPRINT",FACE,{"disambiguationData":[TD([[makeQuery(id+"F11.imprint","IMPRINT",EDGE,{"derivedFrom":sQuery(id+"F11.wireOp",EDGE,"E90.MirrorC")}),1.0]])]});
            var Q1;
            {var subQ5=sQuery(id+"F11.wireOp",EDGE,"E87.left");var subQ6=sQuery(id+"F11.wireOp",EDGE,"E87.bottom");var subQ7=makeQuery(id+"F11.imprint","INTERSECT",VERTEX,{"derivedFrom":[subQ6,subQ5]});Q1=makeQuery(id+"F11.imprint","IMPRINT",FACE,{"disambiguationData":[TD([[makeQuery(id+"F11.imprint","IMPRINT",EDGE,{"disambiguationData":[TD([[subQ7,-1.0]])],"derivedFrom":subQ6}),1.0]])]});}
            var Q2;
            {var subQ7=sQuery(id+"F11.wireOp",EDGE,"E87.right");var subQ8=sQuery(id+"F11.wireOp",EDGE,"E87.bottom");var subQ9=makeQuery(id+"F11.imprint","INTERSECT",VERTEX,{"derivedFrom":[subQ8,subQ7]});Q2=makeQuery(id+"F11.imprint","IMPRINT",FACE,{"disambiguationData":[TD([[makeQuery(id+"F11.imprint","IMPRINT",EDGE,{"disambiguationData":[TD([[subQ9,1.0]])],"derivedFrom":subQ8}),1.0]])]});}
            var Q3;
            Q3=makeQuery(id+"F11.imprint","IMPRINT",FACE,{"disambiguationData":[TD([[makeQuery(id+"F11.imprint","IMPRINT",EDGE,{"derivedFrom":sQuery(id+"F11.wireOp",EDGE,"E91.MirrorC")}),-1.0]])]});
            var Q4;
            Q4=makeQuery(id+"F11.imprint","IMPRINT",FACE,{"disambiguationData":[TD([[makeQuery(id+"F11.imprint","IMPRINT",EDGE,{"derivedFrom":sQuery(id+"F11.wireOp",EDGE,"E89.MirrorC")}),1.0]])]});
            var Q5;
            {var subQ7=sQuery(id+"F11.wireOp",EDGE,"E87.right");var subQ8=sQuery(id+"F11.wireOp",EDGE,"E87.top");var subQ9=makeQuery(id+"F11.imprint","INTERSECT",VERTEX,{"derivedFrom":[subQ8,subQ7]});Q5=makeQuery(id+"F11.imprint","IMPRINT",FACE,{"disambiguationData":[TD([[makeQuery(id+"F11.imprint","IMPRINT",EDGE,{"disambiguationData":[TD([[subQ9,1.0]])],"derivedFrom":subQ8}),-1.0]])]});}
            var Q6;
            Q6=makeQuery(id+"F11.imprint","IMPRINT",FACE,{"disambiguationData":[TD([[makeQuery(id+"F11.imprint","IMPRINT",EDGE,{"derivedFrom":sQuery(id+"F11.wireOp",EDGE,"E88")}),-1.0]])]});
            var Q7;
            {var subQ7=sQuery(id+"F11.wireOp",EDGE,"E87.left");var subQ9=sQuery(id+"F11.wireOp",EDGE,"E87.top");var subQ10=makeQuery(id+"F11.imprint","INTERSECT",VERTEX,{"derivedFrom":[subQ9,subQ7]});Q7=makeQuery(id+"F11.imprint","IMPRINT",FACE,{"disambiguationData":[TD([[makeQuery(id+"F11.imprint","IMPRINT",EDGE,{"disambiguationData":[TD([[subQ10,-1.0]])],"derivedFrom":subQ9}),-1.0]])]});}
            extrude(context, id + "F12", {"entities" : qUnion([Q0, Q1, Q2, Q3, Q4, Q5, Q6, Q7]), "operationType" : NewBodyOperationType.REMOVE, "oppositeDirection" : true, "depth" : 4.83 * mm, "offsetDistance" : 25.4 * mm});
        }
        {
            var Q0;
            {var subQ11=sQuery(id+"F11.wireOp",EDGE,"E99.MirrorCS");var subQ12=sQuery(id+"F11.wireOp",EDGE,"E87.bottom");var subQ13=makeQuery(id+"F11.imprint","INTERSECT",VERTEX,{"derivedFrom":[subQ12,subQ11]});Q0=makeQuery(id+"F11.imprint","IMPRINT",FACE,{"disambiguationData":[TD([[makeQuery(id+"F11.imprint","IMPRINT",EDGE,{"disambiguationData":[TD([[subQ13,-1.0]])],"derivedFrom":subQ12}),-1.0]])]});}
            var Q1;
            Q1=makeQuery(id+"F11.imprint","IMPRINT",FACE,{"disambiguationData":[TD([[makeQuery(id+"F11.imprint","IMPRINT",EDGE,{"derivedFrom":sQuery(id+"F11.wireOp",EDGE,"E91.MirrorC")}),1.0]])]});
            var Q2;
            {var subQ0=sQuery(id+"F11.wireOp",EDGE,"E99.MirrorCS");var subQ1=sQuery(id+"F11.wireOp",EDGE,"E87.bottom");var subQ2=makeQuery(id+"F11.imprint","INTERSECT",VERTEX,{"derivedFrom":[subQ1,subQ0]});Q2=makeQuery(id+"F11.imprint","IMPRINT",FACE,{"disambiguationData":[TD([[makeQuery(id+"F11.imprint","IMPRINT",EDGE,{"disambiguationData":[TD([[subQ2,-1.0]])],"derivedFrom":subQ1}),1.0]])]});}
            var Q3;
            {var subQ0=sQuery(id+"F11.wireOp",EDGE,"E104.MirrorCS");var subQ1=sQuery(id+"F11.wireOp",EDGE,"E87.right");var subQ2=makeQuery(id+"F11.imprint","INTERSECT",VERTEX,{"derivedFrom":[subQ1,subQ0]});Q3=makeQuery(id+"F11.imprint","IMPRINT",FACE,{"disambiguationData":[TD([[makeQuery(id+"F11.imprint","IMPRINT",EDGE,{"disambiguationData":[TD([[subQ2,1.0]])],"derivedFrom":subQ1}),1.0]])]});}
            var Q4;
            {var subQ0=sQuery(id+"F11.wireOp",EDGE,"E101.MirrorCS");var subQ1=sQuery(id+"F11.wireOp",EDGE,"E87.right");var subQ2=makeQuery(id+"F11.imprint","INTERSECT",VERTEX,{"derivedFrom":[subQ1,subQ0]});Q4=makeQuery(id+"F11.imprint","IMPRINT",FACE,{"disambiguationData":[TD([[makeQuery(id+"F11.imprint","IMPRINT",EDGE,{"disambiguationData":[TD([[subQ2,-1.0]])],"derivedFrom":subQ1}),1.0]])]});}
            var Q5;
            Q5=makeQuery(id+"F11.imprint","IMPRINT",FACE,{"disambiguationData":[TD([[makeQuery(id+"F11.imprint","IMPRINT",EDGE,{"derivedFrom":sQuery(id+"F11.wireOp",EDGE,"E89.MirrorC")}),-1.0]])]});
            var Q6;
            {var subQ0=sQuery(id+"F11.wireOp",EDGE,"E97.MirrorCS");var subQ1=sQuery(id+"F11.wireOp",EDGE,"E87.top");var subQ2=makeQuery(id+"F11.imprint","INTERSECT",VERTEX,{"derivedFrom":[subQ1,subQ0]});Q6=makeQuery(id+"F11.imprint","IMPRINT",FACE,{"disambiguationData":[TD([[makeQuery(id+"F11.imprint","IMPRINT",EDGE,{"disambiguationData":[TD([[subQ2,-1.0]])],"derivedFrom":subQ1}),-1.0]])]});}
            var Q7;
            {var subQ0=sQuery(id+"F11.wireOp",EDGE,"E102.MirrorCS");var subQ1=sQuery(id+"F11.wireOp",EDGE,"E87.right");var subQ2=makeQuery(id+"F11.imprint","INTERSECT",VERTEX,{"derivedFrom":[subQ1,subQ0]});Q7=makeQuery(id+"F11.imprint","IMPRINT",FACE,{"disambiguationData":[TD([[makeQuery(id+"F11.imprint","IMPRINT",EDGE,{"disambiguationData":[TD([[subQ2,-1.0]])],"derivedFrom":subQ1}),1.0]])]});}
            var Q8;
            {var subQ0=sQuery(id+"F11.wireOp",EDGE,"E100.MirrorCS");var subQ1=sQuery(id+"F11.wireOp",EDGE,"E87.right");var subQ2=makeQuery(id+"F11.imprint","INTERSECT",VERTEX,{"derivedFrom":[subQ1,subQ0]});Q8=makeQuery(id+"F11.imprint","IMPRINT",FACE,{"disambiguationData":[TD([[makeQuery(id+"F11.imprint","IMPRINT",EDGE,{"disambiguationData":[TD([[subQ2,-1.0]])],"derivedFrom":subQ1}),1.0]])]});}
            var Q9;
            {var subQ0=sQuery(id+"F11.wireOp",EDGE,"E104.MirrorCS");var subQ1=sQuery(id+"F11.wireOp",EDGE,"E87.right");var subQ2=makeQuery(id+"F11.imprint","INTERSECT",VERTEX,{"derivedFrom":[subQ1,subQ0]});Q9=makeQuery(id+"F11.imprint","IMPRINT",FACE,{"disambiguationData":[TD([[makeQuery(id+"F11.imprint","IMPRINT",EDGE,{"disambiguationData":[TD([[subQ2,-1.0]])],"derivedFrom":subQ1}),1.0]])]});}
            var Q10;
            Q10=makeQuery(id+"F11.imprint","IMPRINT",FACE,{"disambiguationData":[TD([[makeQuery(id+"F11.imprint","IMPRINT",EDGE,{"derivedFrom":sQuery(id+"F11.wireOp",EDGE,"E88")}),1.0]])]});
            var Q11;
            {var subQ0=sQuery(id+"F11.wireOp",EDGE,"E98.MirrorCS");var subQ1=sQuery(id+"F11.wireOp",EDGE,"E87.left");var subQ2=makeQuery(id+"F11.imprint","INTERSECT",VERTEX,{"derivedFrom":[subQ1,subQ0]});Q11=makeQuery(id+"F11.imprint","IMPRINT",FACE,{"disambiguationData":[TD([[makeQuery(id+"F11.imprint","IMPRINT",EDGE,{"disambiguationData":[TD([[subQ2,-1.0]])],"derivedFrom":subQ1}),-1.0]])]});}
            var Q12;
            Q12=makeQuery(id+"F11.imprint","IMPRINT",FACE,{"disambiguationData":[TD([[makeQuery(id+"F11.imprint","IMPRINT",EDGE,{"derivedFrom":sQuery(id+"F11.wireOp",EDGE,"E90.MirrorC")}),-1.0]])]});
            extrude(context, id + "F13", {"entities" : qUnion([Q0, Q1, Q2, Q3, Q4, Q5, Q6, Q7, Q8, Q9, Q10, Q11, Q12]), "operationType" : NewBodyOperationType.REMOVE, "oppositeDirection" : true, "depth" : 76.2 * mm, "offsetDistance" : 25.4 * mm});
        }
        {
            var Q0;
            {var subQ5=sQuery(id+"F10.wireOp",EDGE,"E66.left");var subQ6=sQuery(id+"F10.wireOp",EDGE,"E66.bottom");var subQ7=makeQuery(id+"F10.imprint","INTERSECT",VERTEX,{"derivedFrom":[subQ6,subQ5]});Q0=makeQuery(id+"F10.imprint","IMPRINT",FACE,{"disambiguationData":[TD([[makeQuery(id+"F10.imprint","IMPRINT",EDGE,{"disambiguationData":[TD([[subQ7,-1.0]])],"derivedFrom":subQ6}),1.0]])]});}
            var Q1;
            Q1=makeQuery(id+"F10.imprint","IMPRINT",FACE,{"disambiguationData":[TD([[makeQuery(id+"F10.imprint","IMPRINT",EDGE,{"derivedFrom":sQuery(id+"F10.wireOp",EDGE,"E69.MirrorC")}),1.0]])]});
            var Q2;
            {var subQ7=sQuery(id+"F10.wireOp",EDGE,"E66.right");var subQ8=sQuery(id+"F10.wireOp",EDGE,"E66.bottom");var subQ9=makeQuery(id+"F10.imprint","INTERSECT",VERTEX,{"derivedFrom":[subQ8,subQ7]});Q2=makeQuery(id+"F10.imprint","IMPRINT",FACE,{"disambiguationData":[TD([[makeQuery(id+"F10.imprint","IMPRINT",EDGE,{"disambiguationData":[TD([[subQ9,1.0]])],"derivedFrom":subQ8}),1.0]])]});}
            var Q3;
            Q3=makeQuery(id+"F10.imprint","IMPRINT",FACE,{"disambiguationData":[TD([[makeQuery(id+"F10.imprint","IMPRINT",EDGE,{"derivedFrom":sQuery(id+"F10.wireOp",EDGE,"E70.MirrorC")}),-1.0]])]});
            var Q4;
            Q4=makeQuery(id+"F10.imprint","IMPRINT",FACE,{"disambiguationData":[TD([[makeQuery(id+"F10.imprint","IMPRINT",EDGE,{"derivedFrom":sQuery(id+"F10.wireOp",EDGE,"E68.MirrorC")}),1.0]])]});
            var Q5;
            {var subQ7=sQuery(id+"F10.wireOp",EDGE,"E66.right");var subQ8=sQuery(id+"F10.wireOp",EDGE,"E66.top");var subQ9=makeQuery(id+"F10.imprint","INTERSECT",VERTEX,{"derivedFrom":[subQ8,subQ7]});Q5=makeQuery(id+"F10.imprint","IMPRINT",FACE,{"disambiguationData":[TD([[makeQuery(id+"F10.imprint","IMPRINT",EDGE,{"disambiguationData":[TD([[subQ9,1.0]])],"derivedFrom":subQ8}),-1.0]])]});}
            var Q6;
            {var subQ7=sQuery(id+"F10.wireOp",EDGE,"E66.left");var subQ9=sQuery(id+"F10.wireOp",EDGE,"E66.top");var subQ10=makeQuery(id+"F10.imprint","INTERSECT",VERTEX,{"derivedFrom":[subQ9,subQ7]});Q6=makeQuery(id+"F10.imprint","IMPRINT",FACE,{"disambiguationData":[TD([[makeQuery(id+"F10.imprint","IMPRINT",EDGE,{"disambiguationData":[TD([[subQ10,-1.0]])],"derivedFrom":subQ9}),-1.0]])]});}
            var Q7;
            Q7=makeQuery(id+"F10.imprint","IMPRINT",FACE,{"disambiguationData":[TD([[makeQuery(id+"F10.imprint","IMPRINT",EDGE,{"derivedFrom":sQuery(id+"F10.wireOp",EDGE,"E67")}),-1.0]])]});
            extrude(context, id + "F14", {"entities" : qUnion([Q0, Q1, Q2, Q3, Q4, Q5, Q6, Q7]), "operationType" : NewBodyOperationType.REMOVE, "oppositeDirection" : true, "depth" : 4.83 * mm, "offsetDistance" : 25.4 * mm});
        }
        {
            var Q0;
            {var subQ11=sQuery(id+"F10.wireOp",EDGE,"E78.MirrorCS");var subQ12=sQuery(id+"F10.wireOp",EDGE,"E66.bottom");var subQ13=makeQuery(id+"F10.imprint","INTERSECT",VERTEX,{"derivedFrom":[subQ12,subQ11]});Q0=makeQuery(id+"F10.imprint","IMPRINT",FACE,{"disambiguationData":[TD([[makeQuery(id+"F10.imprint","IMPRINT",EDGE,{"disambiguationData":[TD([[subQ13,-1.0]])],"derivedFrom":subQ12}),-1.0]])]});}
            var Q1;
            {var subQ0=sQuery(id+"F10.wireOp",EDGE,"E78.MirrorCS");var subQ1=sQuery(id+"F10.wireOp",EDGE,"E66.bottom");var subQ2=makeQuery(id+"F10.imprint","INTERSECT",VERTEX,{"derivedFrom":[subQ1,subQ0]});Q1=makeQuery(id+"F10.imprint","IMPRINT",FACE,{"disambiguationData":[TD([[makeQuery(id+"F10.imprint","IMPRINT",EDGE,{"disambiguationData":[TD([[subQ2,-1.0]])],"derivedFrom":subQ1}),1.0]])]});}
            var Q2;
            {var subQ0=sQuery(id+"F10.wireOp",EDGE,"E77.MirrorCS");var subQ1=sQuery(id+"F10.wireOp",EDGE,"E66.left");var subQ2=makeQuery(id+"F10.imprint","INTERSECT",VERTEX,{"derivedFrom":[subQ1,subQ0]});Q2=makeQuery(id+"F10.imprint","IMPRINT",FACE,{"disambiguationData":[TD([[makeQuery(id+"F10.imprint","IMPRINT",EDGE,{"disambiguationData":[TD([[subQ2,-1.0]])],"derivedFrom":subQ1}),-1.0]])]});}
            var Q3;
            {var subQ0=sQuery(id+"F10.wireOp",EDGE,"E76.MirrorCS");var subQ1=sQuery(id+"F10.wireOp",EDGE,"E66.top");var subQ2=makeQuery(id+"F10.imprint","INTERSECT",VERTEX,{"derivedFrom":[subQ1,subQ0]});Q3=makeQuery(id+"F10.imprint","IMPRINT",FACE,{"disambiguationData":[TD([[makeQuery(id+"F10.imprint","IMPRINT",EDGE,{"disambiguationData":[TD([[subQ2,-1.0]])],"derivedFrom":subQ1}),-1.0]])]});}
            var Q4;
            {var subQ0=sQuery(id+"F10.wireOp",EDGE,"E80.MirrorCS");var subQ1=sQuery(id+"F10.wireOp",EDGE,"E66.right");var subQ2=makeQuery(id+"F10.imprint","INTERSECT",VERTEX,{"derivedFrom":[subQ1,subQ0]});Q4=makeQuery(id+"F10.imprint","IMPRINT",FACE,{"disambiguationData":[TD([[makeQuery(id+"F10.imprint","IMPRINT",EDGE,{"disambiguationData":[TD([[subQ2,-1.0]])],"derivedFrom":subQ1}),1.0]])]});}
            var Q5;
            {var subQ0=sQuery(id+"F10.wireOp",EDGE,"E81.MirrorCS");var subQ1=sQuery(id+"F10.wireOp",EDGE,"E66.right");var subQ2=makeQuery(id+"F10.imprint","INTERSECT",VERTEX,{"derivedFrom":[subQ1,subQ0]});Q5=makeQuery(id+"F10.imprint","IMPRINT",FACE,{"disambiguationData":[TD([[makeQuery(id+"F10.imprint","IMPRINT",EDGE,{"disambiguationData":[TD([[subQ2,-1.0]])],"derivedFrom":subQ1}),1.0]])]});}
            var Q6;
            {var subQ0=sQuery(id+"F10.wireOp",EDGE,"E79.MirrorCS");var subQ1=sQuery(id+"F10.wireOp",EDGE,"E66.right");var subQ2=makeQuery(id+"F10.imprint","INTERSECT",VERTEX,{"derivedFrom":[subQ1,subQ0]});Q6=makeQuery(id+"F10.imprint","IMPRINT",FACE,{"disambiguationData":[TD([[makeQuery(id+"F10.imprint","IMPRINT",EDGE,{"disambiguationData":[TD([[subQ2,-1.0]])],"derivedFrom":subQ1}),1.0]])]});}
            var Q7;
            {var subQ0=sQuery(id+"F10.wireOp",EDGE,"E83.MirrorCS");var subQ1=sQuery(id+"F10.wireOp",EDGE,"E66.right");var subQ2=makeQuery(id+"F10.imprint","INTERSECT",VERTEX,{"derivedFrom":[subQ1,subQ0]});Q7=makeQuery(id+"F10.imprint","IMPRINT",FACE,{"disambiguationData":[TD([[makeQuery(id+"F10.imprint","IMPRINT",EDGE,{"disambiguationData":[TD([[subQ2,-1.0]])],"derivedFrom":subQ1}),1.0]])]});}
            var Q8;
            {var subQ0=sQuery(id+"F10.wireOp",EDGE,"E83.MirrorCS");var subQ1=sQuery(id+"F10.wireOp",EDGE,"E66.right");var subQ2=makeQuery(id+"F10.imprint","INTERSECT",VERTEX,{"derivedFrom":[subQ1,subQ0]});Q8=makeQuery(id+"F10.imprint","IMPRINT",FACE,{"disambiguationData":[TD([[makeQuery(id+"F10.imprint","IMPRINT",EDGE,{"disambiguationData":[TD([[subQ2,1.0]])],"derivedFrom":subQ1}),1.0]])]});}
            var Q9;
            Q9=makeQuery(id+"F10.imprint","IMPRINT",FACE,{"disambiguationData":[TD([[makeQuery(id+"F10.imprint","IMPRINT",EDGE,{"derivedFrom":sQuery(id+"F10.wireOp",EDGE,"E69.MirrorC")}),-1.0]])]});
            var Q10;
            Q10=makeQuery(id+"F10.imprint","IMPRINT",FACE,{"disambiguationData":[TD([[makeQuery(id+"F10.imprint","IMPRINT",EDGE,{"derivedFrom":sQuery(id+"F10.wireOp",EDGE,"E70.MirrorC")}),1.0]])]});
            var Q11;
            Q11=makeQuery(id+"F10.imprint","IMPRINT",FACE,{"disambiguationData":[TD([[makeQuery(id+"F10.imprint","IMPRINT",EDGE,{"derivedFrom":sQuery(id+"F10.wireOp",EDGE,"E68.MirrorC")}),-1.0]])]});
            var Q12;
            Q12=makeQuery(id+"F10.imprint","IMPRINT",FACE,{"disambiguationData":[TD([[makeQuery(id+"F10.imprint","IMPRINT",EDGE,{"derivedFrom":sQuery(id+"F10.wireOp",EDGE,"E67")}),1.0]])]});
            extrude(context, id + "F15", {"entities" : qUnion([Q0, Q1, Q2, Q3, Q4, Q5, Q6, Q7, Q8, Q9, Q10, Q11, Q12]), "operationType" : NewBodyOperationType.REMOVE, "oppositeDirection" : true, "depth" : 50.8 * mm, "offsetDistance" : 25.4 * mm});
        }
        {
            var Q0;
            {var subQ5=sQuery(id+"F9.wireOp",EDGE,"E45.left");var subQ6=sQuery(id+"F9.wireOp",EDGE,"E45.bottom");var subQ7=makeQuery(id+"F9.imprint","INTERSECT",VERTEX,{"derivedFrom":[subQ6,subQ5]});Q0=makeQuery(id+"F9.imprint","IMPRINT",FACE,{"disambiguationData":[TD([[makeQuery(id+"F9.imprint","IMPRINT",EDGE,{"disambiguationData":[TD([[subQ7,-1.0]])],"derivedFrom":subQ6}),1.0]])]});}
            var Q1;
            Q1=makeQuery(id+"F9.imprint","IMPRINT",FACE,{"disambiguationData":[TD([[makeQuery(id+"F9.imprint","IMPRINT",EDGE,{"derivedFrom":sQuery(id+"F9.wireOp",EDGE,"E48.MirrorC")}),1.0]])]});
            var Q2;
            {var subQ7=sQuery(id+"F9.wireOp",EDGE,"E45.right");var subQ8=sQuery(id+"F9.wireOp",EDGE,"E45.bottom");var subQ9=makeQuery(id+"F9.imprint","INTERSECT",VERTEX,{"derivedFrom":[subQ8,subQ7]});Q2=makeQuery(id+"F9.imprint","IMPRINT",FACE,{"disambiguationData":[TD([[makeQuery(id+"F9.imprint","IMPRINT",EDGE,{"disambiguationData":[TD([[subQ9,1.0]])],"derivedFrom":subQ8}),1.0]])]});}
            var Q3;
            Q3=makeQuery(id+"F9.imprint","IMPRINT",FACE,{"disambiguationData":[TD([[makeQuery(id+"F9.imprint","IMPRINT",EDGE,{"derivedFrom":sQuery(id+"F9.wireOp",EDGE,"E49.MirrorC")}),-1.0]])]});
            var Q4;
            {var subQ7=sQuery(id+"F9.wireOp",EDGE,"E45.right");var subQ8=sQuery(id+"F9.wireOp",EDGE,"E45.top");var subQ9=makeQuery(id+"F9.imprint","INTERSECT",VERTEX,{"derivedFrom":[subQ8,subQ7]});Q4=makeQuery(id+"F9.imprint","IMPRINT",FACE,{"disambiguationData":[TD([[makeQuery(id+"F9.imprint","IMPRINT",EDGE,{"disambiguationData":[TD([[subQ9,1.0]])],"derivedFrom":subQ8}),-1.0]])]});}
            var Q5;
            Q5=makeQuery(id+"F9.imprint","IMPRINT",FACE,{"disambiguationData":[TD([[makeQuery(id+"F9.imprint","IMPRINT",EDGE,{"derivedFrom":sQuery(id+"F9.wireOp",EDGE,"E47.MirrorC")}),1.0]])]});
            var Q6;
            {var subQ7=sQuery(id+"F9.wireOp",EDGE,"E45.left");var subQ9=sQuery(id+"F9.wireOp",EDGE,"E45.top");var subQ10=makeQuery(id+"F9.imprint","INTERSECT",VERTEX,{"derivedFrom":[subQ9,subQ7]});Q6=makeQuery(id+"F9.imprint","IMPRINT",FACE,{"disambiguationData":[TD([[makeQuery(id+"F9.imprint","IMPRINT",EDGE,{"disambiguationData":[TD([[subQ10,-1.0]])],"derivedFrom":subQ9}),-1.0]])]});}
            var Q7;
            Q7=makeQuery(id+"F9.imprint","IMPRINT",FACE,{"disambiguationData":[TD([[makeQuery(id+"F9.imprint","IMPRINT",EDGE,{"derivedFrom":sQuery(id+"F9.wireOp",EDGE,"E46")}),-1.0]])]});
            extrude(context, id + "F16", {"entities" : qUnion([Q0, Q1, Q2, Q3, Q4, Q5, Q6, Q7]), "operationType" : NewBodyOperationType.REMOVE, "oppositeDirection" : true, "depth" : 4.83 * mm, "offsetDistance" : 25.4 * mm});
        }
        {
            var Q0;
            {var subQ11=sQuery(id+"F9.wireOp",EDGE,"E57.MirrorCS");var subQ12=sQuery(id+"F9.wireOp",EDGE,"E45.bottom");var subQ13=makeQuery(id+"F9.imprint","INTERSECT",VERTEX,{"derivedFrom":[subQ12,subQ11]});Q0=makeQuery(id+"F9.imprint","IMPRINT",FACE,{"disambiguationData":[TD([[makeQuery(id+"F9.imprint","IMPRINT",EDGE,{"disambiguationData":[TD([[subQ13,-1.0]])],"derivedFrom":subQ12}),-1.0]])]});}
            var Q1;
            {var subQ0=sQuery(id+"F9.wireOp",EDGE,"E55.MirrorCS");var subQ1=sQuery(id+"F9.wireOp",EDGE,"E45.top");var subQ2=makeQuery(id+"F9.imprint","INTERSECT",VERTEX,{"derivedFrom":[subQ1,subQ0]});Q1=makeQuery(id+"F9.imprint","IMPRINT",FACE,{"disambiguationData":[TD([[makeQuery(id+"F9.imprint","IMPRINT",EDGE,{"disambiguationData":[TD([[subQ2,-1.0]])],"derivedFrom":subQ1}),-1.0]])]});}
            var Q2;
            {var subQ0=sQuery(id+"F9.wireOp",EDGE,"E56.MirrorCS");var subQ1=sQuery(id+"F9.wireOp",EDGE,"E45.left");var subQ2=makeQuery(id+"F9.imprint","INTERSECT",VERTEX,{"derivedFrom":[subQ1,subQ0]});Q2=makeQuery(id+"F9.imprint","IMPRINT",FACE,{"disambiguationData":[TD([[makeQuery(id+"F9.imprint","IMPRINT",EDGE,{"disambiguationData":[TD([[subQ2,-1.0]])],"derivedFrom":subQ1}),-1.0]])]});}
            var Q3;
            {var subQ0=sQuery(id+"F9.wireOp",EDGE,"E59.MirrorCS");var subQ1=sQuery(id+"F9.wireOp",EDGE,"E45.right");var subQ2=makeQuery(id+"F9.imprint","INTERSECT",VERTEX,{"derivedFrom":[subQ1,subQ0]});Q3=makeQuery(id+"F9.imprint","IMPRINT",FACE,{"disambiguationData":[TD([[makeQuery(id+"F9.imprint","IMPRINT",EDGE,{"disambiguationData":[TD([[subQ2,-1.0]])],"derivedFrom":subQ1}),1.0]])]});}
            var Q4;
            {var subQ0=sQuery(id+"F9.wireOp",EDGE,"E60.MirrorCS");var subQ1=sQuery(id+"F9.wireOp",EDGE,"E45.right");var subQ2=makeQuery(id+"F9.imprint","INTERSECT",VERTEX,{"derivedFrom":[subQ1,subQ0]});Q4=makeQuery(id+"F9.imprint","IMPRINT",FACE,{"disambiguationData":[TD([[makeQuery(id+"F9.imprint","IMPRINT",EDGE,{"disambiguationData":[TD([[subQ2,-1.0]])],"derivedFrom":subQ1}),1.0]])]});}
            var Q5;
            {var subQ0=sQuery(id+"F9.wireOp",EDGE,"E58.MirrorCS");var subQ1=sQuery(id+"F9.wireOp",EDGE,"E45.right");var subQ2=makeQuery(id+"F9.imprint","INTERSECT",VERTEX,{"derivedFrom":[subQ1,subQ0]});Q5=makeQuery(id+"F9.imprint","IMPRINT",FACE,{"disambiguationData":[TD([[makeQuery(id+"F9.imprint","IMPRINT",EDGE,{"disambiguationData":[TD([[subQ2,-1.0]])],"derivedFrom":subQ1}),1.0]])]});}
            var Q6;
            {var subQ0=sQuery(id+"F9.wireOp",EDGE,"E62.MirrorCS");var subQ1=sQuery(id+"F9.wireOp",EDGE,"E45.right");var subQ2=makeQuery(id+"F9.imprint","INTERSECT",VERTEX,{"derivedFrom":[subQ1,subQ0]});Q6=makeQuery(id+"F9.imprint","IMPRINT",FACE,{"disambiguationData":[TD([[makeQuery(id+"F9.imprint","IMPRINT",EDGE,{"disambiguationData":[TD([[subQ2,-1.0]])],"derivedFrom":subQ1}),1.0]])]});}
            var Q7;
            {var subQ0=sQuery(id+"F9.wireOp",EDGE,"E62.MirrorCS");var subQ1=sQuery(id+"F9.wireOp",EDGE,"E45.right");var subQ2=makeQuery(id+"F9.imprint","INTERSECT",VERTEX,{"derivedFrom":[subQ1,subQ0]});Q7=makeQuery(id+"F9.imprint","IMPRINT",FACE,{"disambiguationData":[TD([[makeQuery(id+"F9.imprint","IMPRINT",EDGE,{"disambiguationData":[TD([[subQ2,1.0]])],"derivedFrom":subQ1}),1.0]])]});}
            var Q8;
            {var subQ0=sQuery(id+"F9.wireOp",EDGE,"E57.MirrorCS");var subQ1=sQuery(id+"F9.wireOp",EDGE,"E45.bottom");var subQ2=makeQuery(id+"F9.imprint","INTERSECT",VERTEX,{"derivedFrom":[subQ1,subQ0]});Q8=makeQuery(id+"F9.imprint","IMPRINT",FACE,{"disambiguationData":[TD([[makeQuery(id+"F9.imprint","IMPRINT",EDGE,{"disambiguationData":[TD([[subQ2,-1.0]])],"derivedFrom":subQ1}),1.0]])]});}
            var Q9;
            Q9=makeQuery(id+"F9.imprint","IMPRINT",FACE,{"disambiguationData":[TD([[makeQuery(id+"F9.imprint","IMPRINT",EDGE,{"derivedFrom":sQuery(id+"F9.wireOp",EDGE,"E47.MirrorC")}),-1.0]])]});
            var Q10;
            Q10=makeQuery(id+"F9.imprint","IMPRINT",FACE,{"disambiguationData":[TD([[makeQuery(id+"F9.imprint","IMPRINT",EDGE,{"derivedFrom":sQuery(id+"F9.wireOp",EDGE,"E49.MirrorC")}),1.0]])]});
            var Q11;
            Q11=makeQuery(id+"F9.imprint","IMPRINT",FACE,{"disambiguationData":[TD([[makeQuery(id+"F9.imprint","IMPRINT",EDGE,{"derivedFrom":sQuery(id+"F9.wireOp",EDGE,"E48.MirrorC")}),-1.0]])]});
            var Q12;
            Q12=makeQuery(id+"F9.imprint","IMPRINT",FACE,{"disambiguationData":[TD([[makeQuery(id+"F9.imprint","IMPRINT",EDGE,{"derivedFrom":sQuery(id+"F9.wireOp",EDGE,"E46")}),1.0]])]});
            extrude(context, id + "F17", {"entities" : qUnion([Q0, Q1, Q2, Q3, Q4, Q5, Q6, Q7, Q8, Q9, Q10, Q11, Q12]), "operationType" : NewBodyOperationType.REMOVE, "oppositeDirection" : true, "depth" : 50.8 * mm, "offsetDistance" : 25.4 * mm});
        }
        {
            var Q0;
            Q0=makeQuery(id+"F8.imprint","IMPRINT",FACE,{"disambiguationData":[TD([[makeQuery(id+"F8.imprint","IMPRINT",EDGE,{"derivedFrom":sQuery(id+"F8.wireOp",EDGE,"E27.MirrorC")}),1.0]])]});
            var Q1;
            {var subQ5=sQuery(id+"F8.wireOp",EDGE,"E24.left");var subQ6=sQuery(id+"F8.wireOp",EDGE,"E24.bottom");var subQ7=makeQuery(id+"F8.imprint","INTERSECT",VERTEX,{"derivedFrom":[subQ6,subQ5]});Q1=makeQuery(id+"F8.imprint","IMPRINT",FACE,{"disambiguationData":[TD([[makeQuery(id+"F8.imprint","IMPRINT",EDGE,{"disambiguationData":[TD([[subQ7,-1.0]])],"derivedFrom":subQ6}),1.0]])]});}
            var Q2;
            {var subQ7=sQuery(id+"F8.wireOp",EDGE,"E24.right");var subQ8=sQuery(id+"F8.wireOp",EDGE,"E24.bottom");var subQ9=makeQuery(id+"F8.imprint","INTERSECT",VERTEX,{"derivedFrom":[subQ8,subQ7]});Q2=makeQuery(id+"F8.imprint","IMPRINT",FACE,{"disambiguationData":[TD([[makeQuery(id+"F8.imprint","IMPRINT",EDGE,{"disambiguationData":[TD([[subQ9,1.0]])],"derivedFrom":subQ8}),1.0]])]});}
            var Q3;
            Q3=makeQuery(id+"F8.imprint","IMPRINT",FACE,{"disambiguationData":[TD([[makeQuery(id+"F8.imprint","IMPRINT",EDGE,{"derivedFrom":sQuery(id+"F8.wireOp",EDGE,"E28.MirrorC")}),-1.0]])]});
            var Q4;
            {var subQ7=sQuery(id+"F8.wireOp",EDGE,"E24.right");var subQ8=sQuery(id+"F8.wireOp",EDGE,"E24.top");var subQ9=makeQuery(id+"F8.imprint","INTERSECT",VERTEX,{"derivedFrom":[subQ8,subQ7]});Q4=makeQuery(id+"F8.imprint","IMPRINT",FACE,{"disambiguationData":[TD([[makeQuery(id+"F8.imprint","IMPRINT",EDGE,{"disambiguationData":[TD([[subQ9,1.0]])],"derivedFrom":subQ8}),-1.0]])]});}
            var Q5;
            Q5=makeQuery(id+"F8.imprint","IMPRINT",FACE,{"disambiguationData":[TD([[makeQuery(id+"F8.imprint","IMPRINT",EDGE,{"derivedFrom":sQuery(id+"F8.wireOp",EDGE,"E26.MirrorC")}),1.0]])]});
            var Q6;
            {var subQ7=sQuery(id+"F8.wireOp",EDGE,"E24.left");var subQ9=sQuery(id+"F8.wireOp",EDGE,"E24.top");var subQ10=makeQuery(id+"F8.imprint","INTERSECT",VERTEX,{"derivedFrom":[subQ9,subQ7]});Q6=makeQuery(id+"F8.imprint","IMPRINT",FACE,{"disambiguationData":[TD([[makeQuery(id+"F8.imprint","IMPRINT",EDGE,{"disambiguationData":[TD([[subQ10,-1.0]])],"derivedFrom":subQ9}),-1.0]])]});}
            var Q7;
            Q7=makeQuery(id+"F8.imprint","IMPRINT",FACE,{"disambiguationData":[TD([[makeQuery(id+"F8.imprint","IMPRINT",EDGE,{"derivedFrom":sQuery(id+"F8.wireOp",EDGE,"E25")}),-1.0]])]});
            extrude(context, id + "F18", {"entities" : qUnion([Q0, Q1, Q2, Q3, Q4, Q5, Q6, Q7]), "operationType" : NewBodyOperationType.REMOVE, "oppositeDirection" : true, "depth" : 4.83 * mm, "offsetDistance" : 25.4 * mm});
        }
        {
            var Q0;
            {var subQ11=sQuery(id+"F8.wireOp",EDGE,"E36.MirrorCS");var subQ12=sQuery(id+"F8.wireOp",EDGE,"E24.bottom");var subQ13=makeQuery(id+"F8.imprint","INTERSECT",VERTEX,{"derivedFrom":[subQ12,subQ11]});Q0=makeQuery(id+"F8.imprint","IMPRINT",FACE,{"disambiguationData":[TD([[makeQuery(id+"F8.imprint","IMPRINT",EDGE,{"disambiguationData":[TD([[subQ13,-1.0]])],"derivedFrom":subQ12}),-1.0]])]});}
            var Q1;
            Q1=makeQuery(id+"F8.imprint","IMPRINT",FACE,{"disambiguationData":[TD([[makeQuery(id+"F8.imprint","IMPRINT",EDGE,{"derivedFrom":sQuery(id+"F8.wireOp",EDGE,"E25")}),1.0]])]});
            var Q2;
            {var subQ0=sQuery(id+"F8.wireOp",EDGE,"E35.MirrorCS");var subQ1=sQuery(id+"F8.wireOp",EDGE,"E24.left");var subQ2=makeQuery(id+"F8.imprint","INTERSECT",VERTEX,{"derivedFrom":[subQ1,subQ0]});Q2=makeQuery(id+"F8.imprint","IMPRINT",FACE,{"disambiguationData":[TD([[makeQuery(id+"F8.imprint","IMPRINT",EDGE,{"disambiguationData":[TD([[subQ2,-1.0]])],"derivedFrom":subQ1}),-1.0]])]});}
            var Q3;
            {var subQ0=sQuery(id+"F8.wireOp",EDGE,"E34.MirrorCS");var subQ1=sQuery(id+"F8.wireOp",EDGE,"E24.top");var subQ2=makeQuery(id+"F8.imprint","INTERSECT",VERTEX,{"derivedFrom":[subQ1,subQ0]});Q3=makeQuery(id+"F8.imprint","IMPRINT",FACE,{"disambiguationData":[TD([[makeQuery(id+"F8.imprint","IMPRINT",EDGE,{"disambiguationData":[TD([[subQ2,-1.0]])],"derivedFrom":subQ1}),-1.0]])]});}
            var Q4;
            {var subQ0=sQuery(id+"F8.wireOp",EDGE,"E38.MirrorCS");var subQ1=sQuery(id+"F8.wireOp",EDGE,"E24.right");var subQ2=makeQuery(id+"F8.imprint","INTERSECT",VERTEX,{"derivedFrom":[subQ1,subQ0]});Q4=makeQuery(id+"F8.imprint","IMPRINT",FACE,{"disambiguationData":[TD([[makeQuery(id+"F8.imprint","IMPRINT",EDGE,{"disambiguationData":[TD([[subQ2,-1.0]])],"derivedFrom":subQ1}),1.0]])]});}
            var Q5;
            Q5=makeQuery(id+"F8.imprint","IMPRINT",FACE,{"disambiguationData":[TD([[makeQuery(id+"F8.imprint","IMPRINT",EDGE,{"derivedFrom":sQuery(id+"F8.wireOp",EDGE,"E26.MirrorC")}),-1.0]])]});
            var Q6;
            {var subQ0=sQuery(id+"F8.wireOp",EDGE,"E39.MirrorCS");var subQ1=sQuery(id+"F8.wireOp",EDGE,"E24.right");var subQ2=makeQuery(id+"F8.imprint","INTERSECT",VERTEX,{"derivedFrom":[subQ1,subQ0]});Q6=makeQuery(id+"F8.imprint","IMPRINT",FACE,{"disambiguationData":[TD([[makeQuery(id+"F8.imprint","IMPRINT",EDGE,{"disambiguationData":[TD([[subQ2,-1.0]])],"derivedFrom":subQ1}),1.0]])]});}
            var Q7;
            {var subQ0=sQuery(id+"F8.wireOp",EDGE,"E37.MirrorCS");var subQ1=sQuery(id+"F8.wireOp",EDGE,"E24.right");var subQ2=makeQuery(id+"F8.imprint","INTERSECT",VERTEX,{"derivedFrom":[subQ1,subQ0]});Q7=makeQuery(id+"F8.imprint","IMPRINT",FACE,{"disambiguationData":[TD([[makeQuery(id+"F8.imprint","IMPRINT",EDGE,{"disambiguationData":[TD([[subQ2,-1.0]])],"derivedFrom":subQ1}),1.0]])]});}
            var Q8;
            {var subQ0=sQuery(id+"F8.wireOp",EDGE,"E41.MirrorCS");var subQ1=sQuery(id+"F8.wireOp",EDGE,"E24.right");var subQ2=makeQuery(id+"F8.imprint","INTERSECT",VERTEX,{"derivedFrom":[subQ1,subQ0]});Q8=makeQuery(id+"F8.imprint","IMPRINT",FACE,{"disambiguationData":[TD([[makeQuery(id+"F8.imprint","IMPRINT",EDGE,{"disambiguationData":[TD([[subQ2,-1.0]])],"derivedFrom":subQ1}),1.0]])]});}
            var Q9;
            {var subQ0=sQuery(id+"F8.wireOp",EDGE,"E41.MirrorCS");var subQ1=sQuery(id+"F8.wireOp",EDGE,"E24.right");var subQ2=makeQuery(id+"F8.imprint","INTERSECT",VERTEX,{"derivedFrom":[subQ1,subQ0]});Q9=makeQuery(id+"F8.imprint","IMPRINT",FACE,{"disambiguationData":[TD([[makeQuery(id+"F8.imprint","IMPRINT",EDGE,{"disambiguationData":[TD([[subQ2,1.0]])],"derivedFrom":subQ1}),1.0]])]});}
            var Q10;
            {var subQ0=sQuery(id+"F8.wireOp",EDGE,"E36.MirrorCS");var subQ1=sQuery(id+"F8.wireOp",EDGE,"E24.bottom");var subQ2=makeQuery(id+"F8.imprint","INTERSECT",VERTEX,{"derivedFrom":[subQ1,subQ0]});Q10=makeQuery(id+"F8.imprint","IMPRINT",FACE,{"disambiguationData":[TD([[makeQuery(id+"F8.imprint","IMPRINT",EDGE,{"disambiguationData":[TD([[subQ2,-1.0]])],"derivedFrom":subQ1}),1.0]])]});}
            var Q11;
            Q11=makeQuery(id+"F8.imprint","IMPRINT",FACE,{"disambiguationData":[TD([[makeQuery(id+"F8.imprint","IMPRINT",EDGE,{"derivedFrom":sQuery(id+"F8.wireOp",EDGE,"E27.MirrorC")}),-1.0]])]});
            var Q12;
            Q12=makeQuery(id+"F8.imprint","IMPRINT",FACE,{"disambiguationData":[TD([[makeQuery(id+"F8.imprint","IMPRINT",EDGE,{"derivedFrom":sQuery(id+"F8.wireOp",EDGE,"E28.MirrorC")}),1.0]])]});
            extrude(context, id + "F19", {"entities" : qUnion([Q0, Q1, Q2, Q3, Q4, Q5, Q6, Q7, Q8, Q9, Q10, Q11, Q12]), "operationType" : NewBodyOperationType.REMOVE, "oppositeDirection" : true, "depth" : 50.8 * mm, "offsetDistance" : 25.4 * mm});
        }
        {
            var Q0;
            {var subQ0=sQuery(id+"F10.wireOp",EDGE,"E82.MirrorCS");Q0=makeQuery(id+"F10.imprint","IMPRINT",FACE,{"disambiguationData":[TD([[makeQuery(id+"F10.imprint","IMPRINT",EDGE,{"derivedFrom":subQ0}),-1.0]])]});}
            var Q1;
            {var subQ5=sQuery(id+"F10.wireOp",EDGE,"E84.MirrorCS");Q1=makeQuery(id+"F10.imprint","IMPRINT",FACE,{"disambiguationData":[TD([[makeQuery(id+"F10.imprint","IMPRINT",EDGE,{"derivedFrom":subQ5}),-1.0]])]});}
            extrude(context, id + "F20", {"entities" : qUnion([Q0, Q1]), "operationType" : NewBodyOperationType.REMOVE, "oppositeDirection" : true, "depth" : 11.18 * mm, "offsetDistance" : 25.4 * mm});
        }
        {
            var Q0;
            {var subQ5=sQuery(id+"F9.wireOp",EDGE,"E63.MirrorCS");Q0=makeQuery(id+"F9.imprint","IMPRINT",FACE,{"disambiguationData":[TD([[makeQuery(id+"F9.imprint","IMPRINT",EDGE,{"derivedFrom":subQ5}),-1.0]])]});}
            var Q1;
            {var subQ0=sQuery(id+"F9.wireOp",EDGE,"E61.MirrorCS");Q1=makeQuery(id+"F9.imprint","IMPRINT",FACE,{"disambiguationData":[TD([[makeQuery(id+"F9.imprint","IMPRINT",EDGE,{"derivedFrom":subQ0}),-1.0]])]});}
            extrude(context, id + "F21", {"entities" : qUnion([Q0, Q1]), "operationType" : NewBodyOperationType.REMOVE, "oppositeDirection" : true, "depth" : 11.18 * mm, "offsetDistance" : 25.4 * mm});
        }
        {
            var Q0;
            {var subQ5=sQuery(id+"F8.wireOp",EDGE,"E42.MirrorCS");Q0=makeQuery(id+"F8.imprint","IMPRINT",FACE,{"disambiguationData":[TD([[makeQuery(id+"F8.imprint","IMPRINT",EDGE,{"derivedFrom":subQ5}),-1.0]])]});}
            var Q1;
            {var subQ0=sQuery(id+"F8.wireOp",EDGE,"E40.MirrorCS");Q1=makeQuery(id+"F8.imprint","IMPRINT",FACE,{"disambiguationData":[TD([[makeQuery(id+"F8.imprint","IMPRINT",EDGE,{"derivedFrom":subQ0}),-1.0]])]});}
            extrude(context, id + "F22", {"entities" : qUnion([Q0, Q1]), "operationType" : NewBodyOperationType.REMOVE, "oppositeDirection" : true, "depth" : 11.18 * mm, "offsetDistance" : 25.4 * mm});
        }
        {
            var Q0;
            {var subQ0=sQuery(id+"F11.wireOp",EDGE,"E103.MirrorCS");Q0=makeQuery(id+"F11.imprint","IMPRINT",FACE,{"disambiguationData":[TD([[makeQuery(id+"F11.imprint","IMPRINT",EDGE,{"derivedFrom":subQ0}),-1.0]])]});}
            var Q1;
            {var subQ5=sQuery(id+"F11.wireOp",EDGE,"E105.MirrorCS");Q1=makeQuery(id+"F11.imprint","IMPRINT",FACE,{"disambiguationData":[TD([[makeQuery(id+"F11.imprint","IMPRINT",EDGE,{"derivedFrom":subQ5}),-1.0]])]});}
            extrude(context, id + "F23", {"entities" : qUnion([Q0, Q1]), "operationType" : NewBodyOperationType.REMOVE, "oppositeDirection" : true, "depth" : 11.18 * mm, "offsetDistance" : 25.4 * mm});
        }
    });
